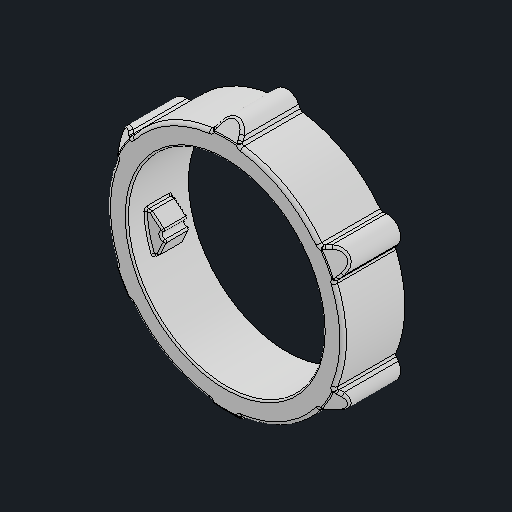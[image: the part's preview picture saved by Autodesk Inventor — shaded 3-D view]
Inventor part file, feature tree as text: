
AUTODESK INVENTOR PART (.ipt)
format: ipt  version: 2024.2 (Build 282272000, 272)  size: 474,624 bytes
history: native  units: mm
features: other x1, fillet x1
ambient origin geometry x8: Origin, YZ Plane, XZ Plane, XY Plane, X Axis, Y Axis, Z Axis, Center Point
bodies: Body1 (feature_tree)
feature tree (2):
  other  "솔리드1"
  fillet  "Fillet4"  [1 undecoded]
note: 1 required parameter value undecoded (feature->parameter linkage not recoverable at this tier; creation-order binding heuristic only, values carry confidence <= 0.55)
